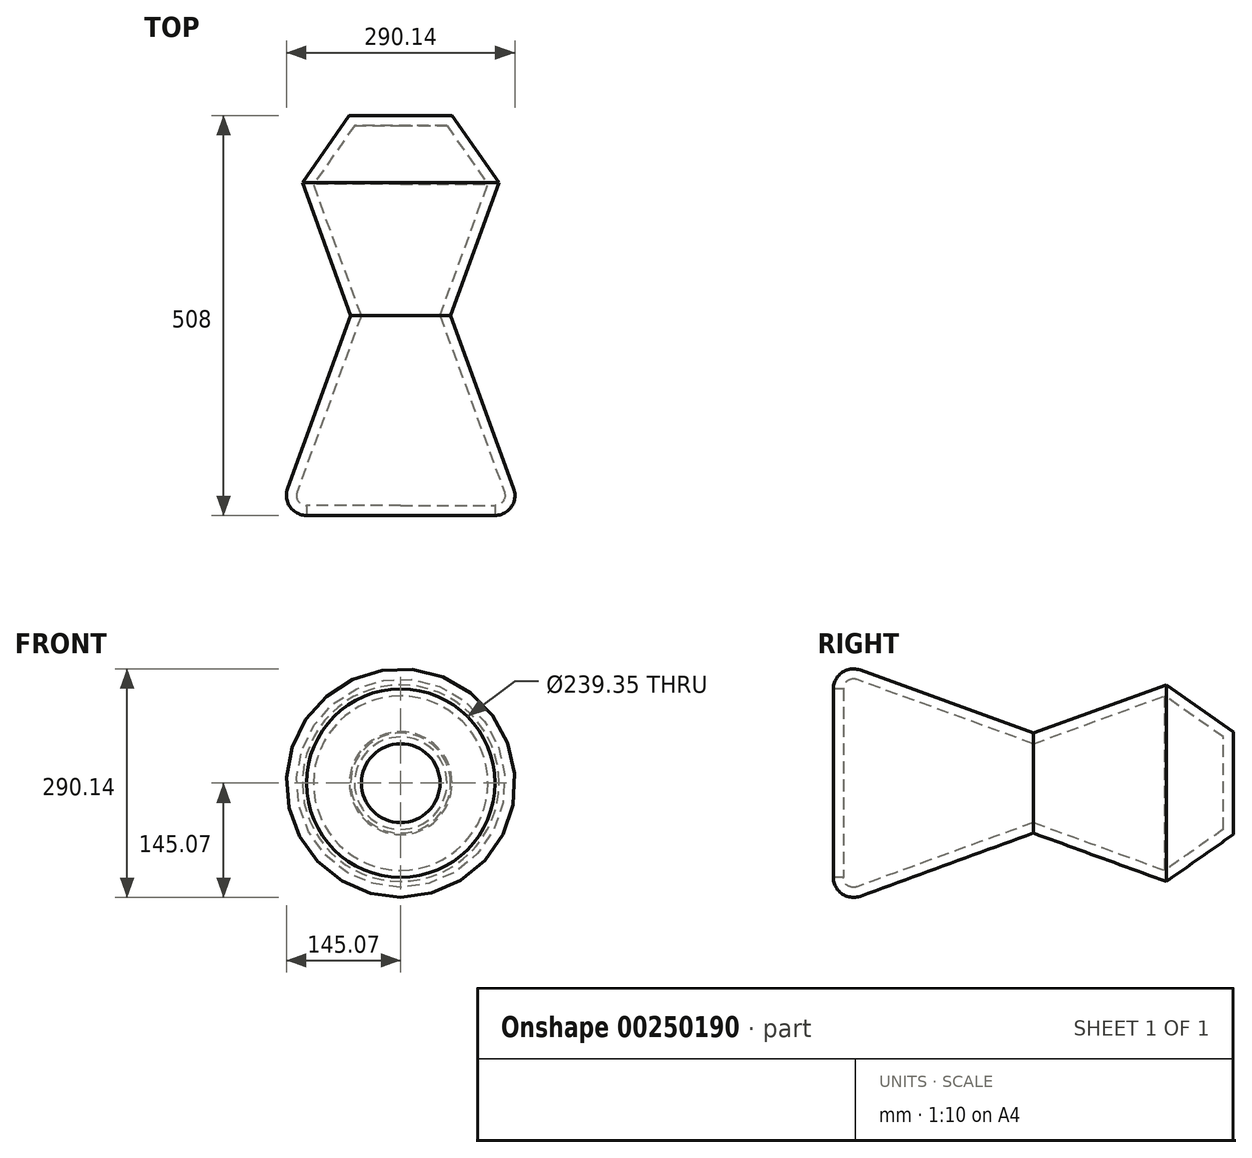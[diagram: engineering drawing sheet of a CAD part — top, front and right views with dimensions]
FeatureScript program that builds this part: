
annotation { "Feature Type Name" : "Feature", "Feature Type Description" : "" }
export const myFeature = defineFeature(function(context is Context, id is Id, definition is map)
    precondition{}
    {
        {
            var Q0;
            Q0=qCreatedBy(makeId("Front.planeOp"),FACE);
            var sketch = newSketch(context, id + "F0", { "sketchPlane" : qUnion([Q0])});
            skCircle(sketch, "E0", {"center": v(0, 0) * mm, "radius": 63.5 * mm});
            skSolve(sketch);
        }
        {
            var Q0;
            Q0=makeQuery(id+"F0.imprint","IMPRINT",FACE,{"disambiguationData":[TD([[makeQuery(id+"F0.imprint","IMPRINT",EDGE,{"derivedFrom":sQuery(id+"F0.wireOp",EDGE,"E0")}),1.0]])]});
            extrude(context, id + "F1", {"entities" : qUnion([Q0]), "depth" : 254 * mm, "hasDraft" : true, "draftAngle" : 20 * degree, "hasSecondDirection" : true, "secondDirectionOppositeDirection" : true, "secondDirectionDepth" : 254 * mm, "hasSecondDirectionDraft" : true, "secondDirectionDraftAngle" : 20 * degree});
        }
        {
            var Q0;
            Q0=makeQuery(id+"F1.opExtrude","CAP_EDGE",EDGE,{"disambiguationData":[OSD([sQuery(id+"F0.wireOp",EDGE,"E0")])],"isStart":false});
            fillet(context, id + "F2", {"entities" : qUnion([Q0]), "radius" : 25.4 * mm, "tangentPropagation" : true, "allowEdgeOverflow" : false});
        }
        {
            var Q0;
            Q0=makeQuery(id+"F1.opExtrude","CAP_EDGE",EDGE,{"disambiguationData":[OSD([sQuery(id+"F0.wireOp",EDGE,"E0")])],"isStart":true});
            chamfer(context, id + "F3", {"entities" : qUnion([Q0]), "width" : 63.5 * mm, "tangentPropagation" : true});
        }
        {
            var Q0;
            Q0=makeQuery(id+"F1.opExtrude","CAP_FACE",FACE,{"disambiguationData":[OSD([sQuery(id+"F0.wireOp",EDGE,"E0")])],"isStart":false});
            shell(context, id + "F4", {"entities" : qUnion([Q0]), "thickness" : 12.7 * mm});
        }
    });
